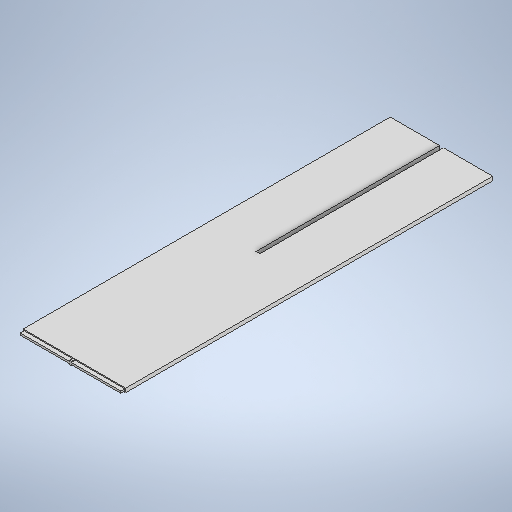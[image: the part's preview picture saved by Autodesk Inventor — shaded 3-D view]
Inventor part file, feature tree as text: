
AUTODESK INVENTOR PART (.ipt)
format: ipt  version: 2025.2 (Build 292293000, 293)  size: 346,112 bytes
history: native  units: mm
features: extrude x9, sketch x9, projected_geometry x1
ambient origin geometry x8: Origin, YZ Plane, XZ Plane, XY Plane, X Axis, Y Axis, Z Axis, Center Point
bodies: Solid1 (feature_tree)
feature tree (19):
  extrude  "Extrusion1"  Depth=447.675mm
  extrude  "Extrusion2"  Depth=4.7625mm TaperAngle=0.0deg
  extrude  "Extrusion3"  Depth=6.0mm
  extrude  "Extrusion4"  Depth=10.0mm TaperAngle=0.0deg
  extrude  "Extrusion5"  Depth=4.763mm
  extrude  "Extrusion6"  Depth=2.374mm
  extrude  "Extrusion7"  Depth=4.763mm
  extrude  "Extrusion8"  Depth=12.5mm
  extrude  "Extrusion9"  Depth=10.0mm TaperAngle=0.0deg
  sketch  "Sketch1"  dims[d0=50.0mm d1=447.675mm]
  sketch  "Sketch2"  dims[d2=4.7625mm d3=0.0mm d9=4.7625mm d10=0.0mm]
  sketch  "Sketch3"  dims[d11=25.0mm d13=6.0mm]
  sketch  "Sketch4"  dims[d14=6.0mm d15=10.0mm d16=0.0mm]
  projected_geometry  "Projected Loop1"
  sketch  "Sketch7"  dims[d17=158.838mm d18=0.0mm d20=4.763mm]
  sketch  "Sketch8"  dims[d21=223.837mm d22=0.0mm d25=2.374mm]
  sketch  "Sketch9"  dims[d26=4.763mm d27=0.0mm d28=25.0mm]
  sketch  "Sketch10"  dims[d29=10.0mm d30=0.0mm d31=12.5mm]
  sketch  "Sketch11"  dims[d32=10.0mm d33=0.0mm d37=10.0mm d38=0.0mm]
